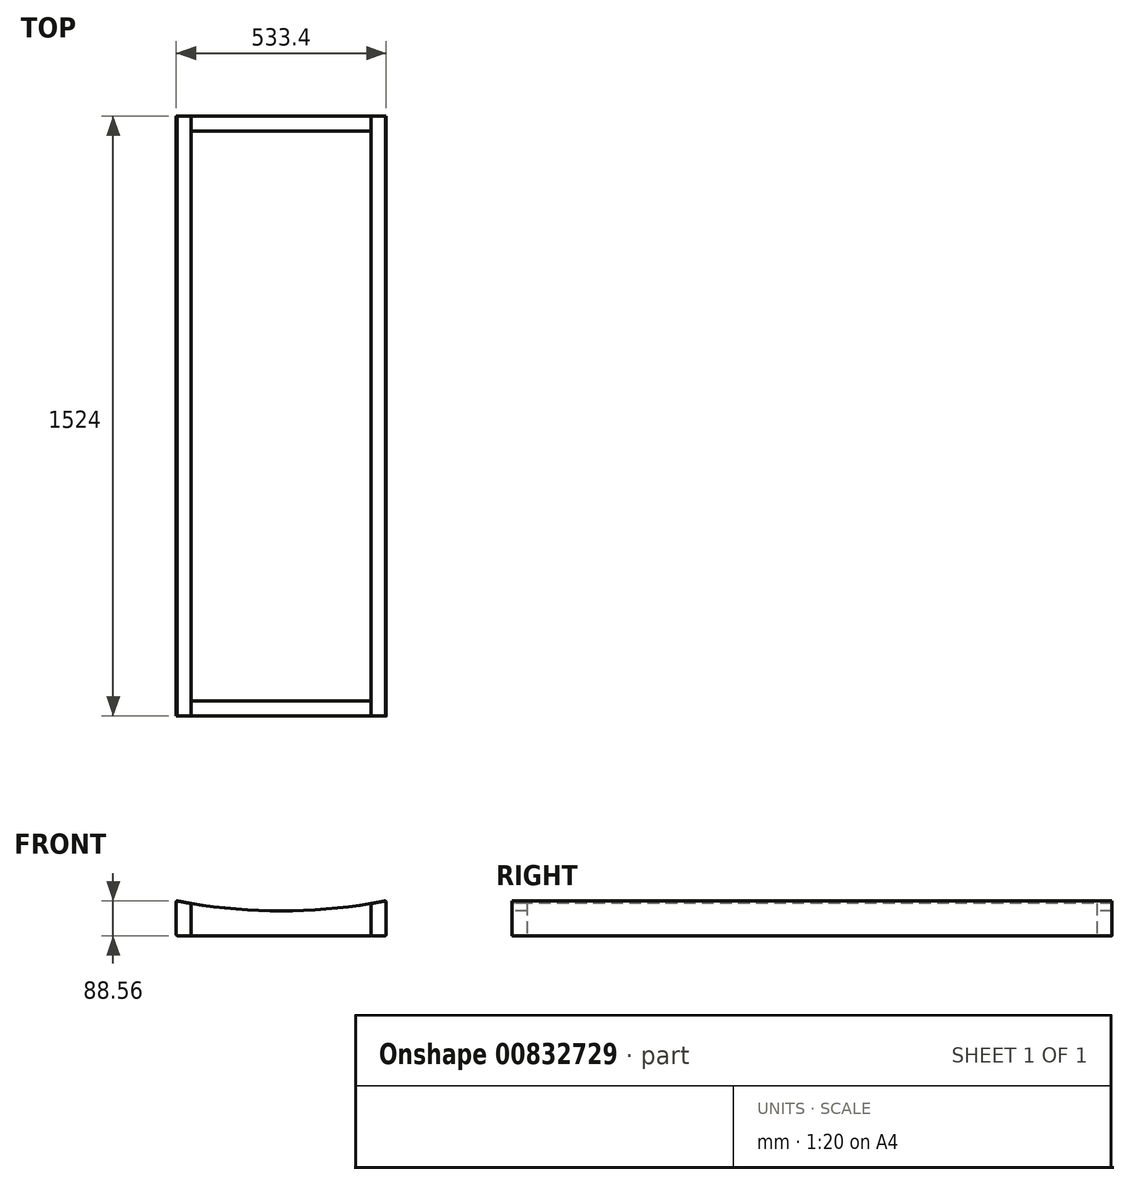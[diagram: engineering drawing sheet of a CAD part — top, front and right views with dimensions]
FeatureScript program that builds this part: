
annotation { "Feature Type Name" : "Feature", "Feature Type Description" : "" }
export const myFeature = defineFeature(function(context is Context, id is Id, definition is map)
    precondition{}
    {
        {
            assignVariable(context, id + "F0", {"name" : "b", "anyValue" : 88.9 * mm});
        }
        {
            var Q0;
            Q0=qCreatedBy(makeId("Top.planeOp"),FACE);
            var sketch = newSketch(context, id + "F1", { "sketchPlane" : qUnion([Q0])});
            skLineSegment(sketch, "E0.bottom", {"start": v(0, 0) * mm, "end": v(533.4, 0) * mm});
            skLineSegment(sketch, "E0.top", {"start": v(0, 1524) * mm, "end": v(533.4, 1524) * mm});
            skLineSegment(sketch, "E0.left", {"start": v(0, 0) * mm, "end": v(0, 1524) * mm});
            skLineSegment(sketch, "E0.right", {"start": v(533.4, 0) * mm, "end": v(533.4, 1524) * mm});
            skLineSegment(sketch, "E1", {"start": v(38.1, 0) * mm, "end": v(38.1, 1524) * mm});
            skLineSegment(sketch, "E2", {"start": v(495.3, 0) * mm, "end": v(495.3, 1524) * mm});
            skLineSegment(sketch, "E3", {"start": v(495.3, 38.1) * mm, "end": v(38.1, 38.1) * mm});
            skLineSegment(sketch, "E4", {"start": v(495.3, 1485.9) * mm, "end": v(38.1, 1485.9) * mm});
            skSolve(sketch);
        }
        {
            var Q0;
            {var subQ0=sQuery(id+"F1.wireOp",EDGE,"E0.left");Q0=makeQuery(id+"F1.imprint","IMPRINT",FACE,{"disambiguationData":[TD([[makeQuery(id+"F1.imprint","IMPRINT",EDGE,{"derivedFrom":subQ0}),-1.0]])]});}
            var Q1;
            {var subQ4=sQuery(id+"F1.wireOp",EDGE,"E0.right");Q1=makeQuery(id+"F1.imprint","IMPRINT",FACE,{"disambiguationData":[TD([[makeQuery(id+"F1.imprint","IMPRINT",EDGE,{"derivedFrom":subQ4}),1.0]])]});}
            var Q2;
            Q2=sQuery(id+"F1.wireOp",EDGE,"E2");
            var Q3;
            Q3=sQuery(id+"F1.wireOp",EDGE,"E0.right");
            var Q4;
            Q4=sQuery(id+"F1.wireOp",EDGE,"E0.left");
            var Q5;
            Q5=sQuery(id+"F1.wireOp",EDGE,"E4");
            var Q6;
            Q6=sQuery(id+"F1.wireOp",EDGE,"E3");
            var Q7;
            Q7=sQuery(id+"F1.wireOp",EDGE,"E0.top");
            var Q8;
            Q8=sQuery(id+"F1.wireOp",EDGE,"E1");
            var Q9;
            Q9=sQuery(id+"F1.wireOp",EDGE,"E0.bottom");
            extrude(context, id + "F2", {"entities" : qUnion([Q0, Q1]), "surfaceEntities" : qUnion([Q2, Q3, Q4, Q5, Q6, Q7, Q8, Q9]), "depth" : getVariable(context, 'b'), "offsetDistance" : 25.4 * mm});
        }
        {
            var Q0;
            {var subQ5=sQuery(id+"F1.wireOp",EDGE,"E3");Q0=makeQuery(id+"F1.imprint","IMPRINT",FACE,{"disambiguationData":[TD([[makeQuery(id+"F1.imprint","IMPRINT",EDGE,{"derivedFrom":subQ5}),1.0]])]});}
            var Q1;
            {var subQ5=sQuery(id+"F1.wireOp",EDGE,"E4");Q1=makeQuery(id+"F1.imprint","IMPRINT",FACE,{"disambiguationData":[TD([[makeQuery(id+"F1.imprint","IMPRINT",EDGE,{"derivedFrom":subQ5}),-1.0]])]});}
            extrude(context, id + "F3", {"entities" : qUnion([Q0, Q1]), "depth" : getVariable(context, 'b'), "offsetDistance" : 25.4 * mm});
        }
        {
            var Q0;
            Q0=makeQuery(id+"F3.opExtrude","CAP_EDGE",EDGE,{"disambiguationData":[OSD([sQuery(id+"F1.wireOp",EDGE,"E0.bottom")])],"isStart":false});
            var Q1;
            Q1=makeQuery(id+"F3.opExtrude","CAP_EDGE",EDGE,{"disambiguationData":[OSD([sQuery(id+"F1.wireOp",EDGE,"E0.bottom")])],"isStart":true});
            var Q2;
            Q2=makeQuery(id+"F3.opExtrude","CAP_EDGE",EDGE,{"disambiguationData":[OSD([sQuery(id+"F1.wireOp",EDGE,"E3")])],"isStart":false});
            var Q3;
            Q3=makeQuery(id+"F3.opExtrude","CAP_EDGE",EDGE,{"disambiguationData":[OSD([sQuery(id+"F1.wireOp",EDGE,"E3")])],"isStart":true});
            var Q4;
            Q4=makeQuery(id+"F2.opExtrude","CAP_EDGE",EDGE,{"disambiguationData":[OSD([sQuery(id+"F1.wireOp",EDGE,"E2")])],"isStart":true});
            var Q5;
            Q5=makeQuery(id+"F2.opExtrude","CAP_EDGE",EDGE,{"disambiguationData":[OSD([sQuery(id+"F1.wireOp",EDGE,"E0.right")])],"isStart":true});
            var Q6;
            Q6=makeQuery(id+"F2.opExtrude","CAP_EDGE",EDGE,{"disambiguationData":[OSD([sQuery(id+"F1.wireOp",EDGE,"E0.right")])],"isStart":false});
            var Q7;
            Q7=makeQuery(id+"F2.opExtrude","CAP_EDGE",EDGE,{"disambiguationData":[OSD([sQuery(id+"F1.wireOp",EDGE,"E2")])],"isStart":false});
            var Q8;
            Q8=makeQuery(id+"F2.opExtrude","CAP_EDGE",EDGE,{"disambiguationData":[OSD([sQuery(id+"F1.wireOp",EDGE,"E1")])],"isStart":false});
            var Q9;
            Q9=makeQuery(id+"F2.opExtrude","CAP_EDGE",EDGE,{"disambiguationData":[OSD([sQuery(id+"F1.wireOp",EDGE,"E1")])],"isStart":true});
            var Q10;
            Q10=makeQuery(id+"F2.opExtrude","CAP_EDGE",EDGE,{"disambiguationData":[OSD([sQuery(id+"F1.wireOp",EDGE,"E0.left")])],"isStart":false});
            var Q11;
            Q11=makeQuery(id+"F2.opExtrude","CAP_EDGE",EDGE,{"disambiguationData":[OSD([sQuery(id+"F1.wireOp",EDGE,"E0.left")])],"isStart":true});
            var Q12;
            Q12=makeQuery(id+"F3.opExtrude","CAP_EDGE",EDGE,{"disambiguationData":[OSD([sQuery(id+"F1.wireOp",EDGE,"E4")])],"isStart":true});
            var Q13;
            Q13=makeQuery(id+"F3.opExtrude","CAP_EDGE",EDGE,{"disambiguationData":[OSD([sQuery(id+"F1.wireOp",EDGE,"E4")])],"isStart":false});
            var Q14;
            Q14=makeQuery(id+"F3.opExtrude","CAP_EDGE",EDGE,{"disambiguationData":[OSD([sQuery(id+"F1.wireOp",EDGE,"E0.top")])],"isStart":false});
            var Q15;
            Q15=makeQuery(id+"F3.opExtrude","CAP_EDGE",EDGE,{"disambiguationData":[OSD([sQuery(id+"F1.wireOp",EDGE,"E0.top")])],"isStart":true});
            fillet(context, id + "F4", {"entities" : qUnion([Q0, Q1, Q2, Q3, Q4, Q5, Q6, Q7, Q8, Q9, Q10, Q11, Q12, Q13, Q14, Q15]), "radius" : 3.17 * mm, "allowEdgeOverflow" : false});
        }
        {
            var Q0;
            Q0=qCreatedBy(makeId("Front.planeOp"),FACE);
            var sketch = newSketch(context, id + "F5", { "sketchPlane" : qUnion([Q0])});
            skCircle(sketch, "E5", {"center": v(266.7, 1476.37) * mm, "radius": 1412.87 * mm});
            skSolve(sketch);
        }
        {
            var Q0;
            Q0=makeQuery(id+"F5.imprint","IMPRINT",FACE,{"disambiguationData":[TD([[makeQuery(id+"F5.imprint","IMPRINT",EDGE,{"derivedFrom":sQuery(id+"F5.wireOp",EDGE,"E5")}),1.0]])]});
            extrude(context, id + "F6", {"entities" : qUnion([Q0]), "operationType" : NewBodyOperationType.REMOVE, "endBound" : BoundingType.THROUGH_ALL, "oppositeDirection" : true, "depth" : 25.4 * mm, "offsetDistance" : 25.4 * mm});
        }
    });
